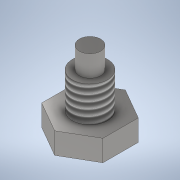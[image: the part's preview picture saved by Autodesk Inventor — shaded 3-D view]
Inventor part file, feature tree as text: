
AUTODESK INVENTOR PART (.ipt)
format: ipt  version: 2020 (Build 240168000, 168)  size: 121,856 bytes
history: native  units: mm
features: extrude x3, sketch x3, thread x1
ambient origin geometry x8: Origin, YZ Plane, XZ Plane, XY Plane, X Axis, Y Axis, Z Axis, Center Point
bodies: Solid1 (feature_tree)
feature tree (7):
  extrude  "Extrusion1"  Depth=1.5mm TaperAngle=0.0deg
  extrude  "Extrusion2"  Depth=2.5mm TaperAngle=0.0deg
  thread  "Thread1"  [1 undecoded]
  extrude  "Extrusion3"  Depth=1.5mm
  sketch  "Sketch1"  dims[d0=5.0mm d1=1.5mm d2=0.0mm]
  sketch  "Sketch2"  dims[d3=2.5mm d4=2.5mm d5=0.0mm d6=2.5mm d7=0.0mm]
  sketch  "Sketch3"  dims[d8=1.5mm d9=0.0mm d10=1.5mm]
note: 1 required parameter value undecoded (feature->parameter linkage not recoverable at this tier; creation-order binding heuristic only, values carry confidence <= 0.55)
